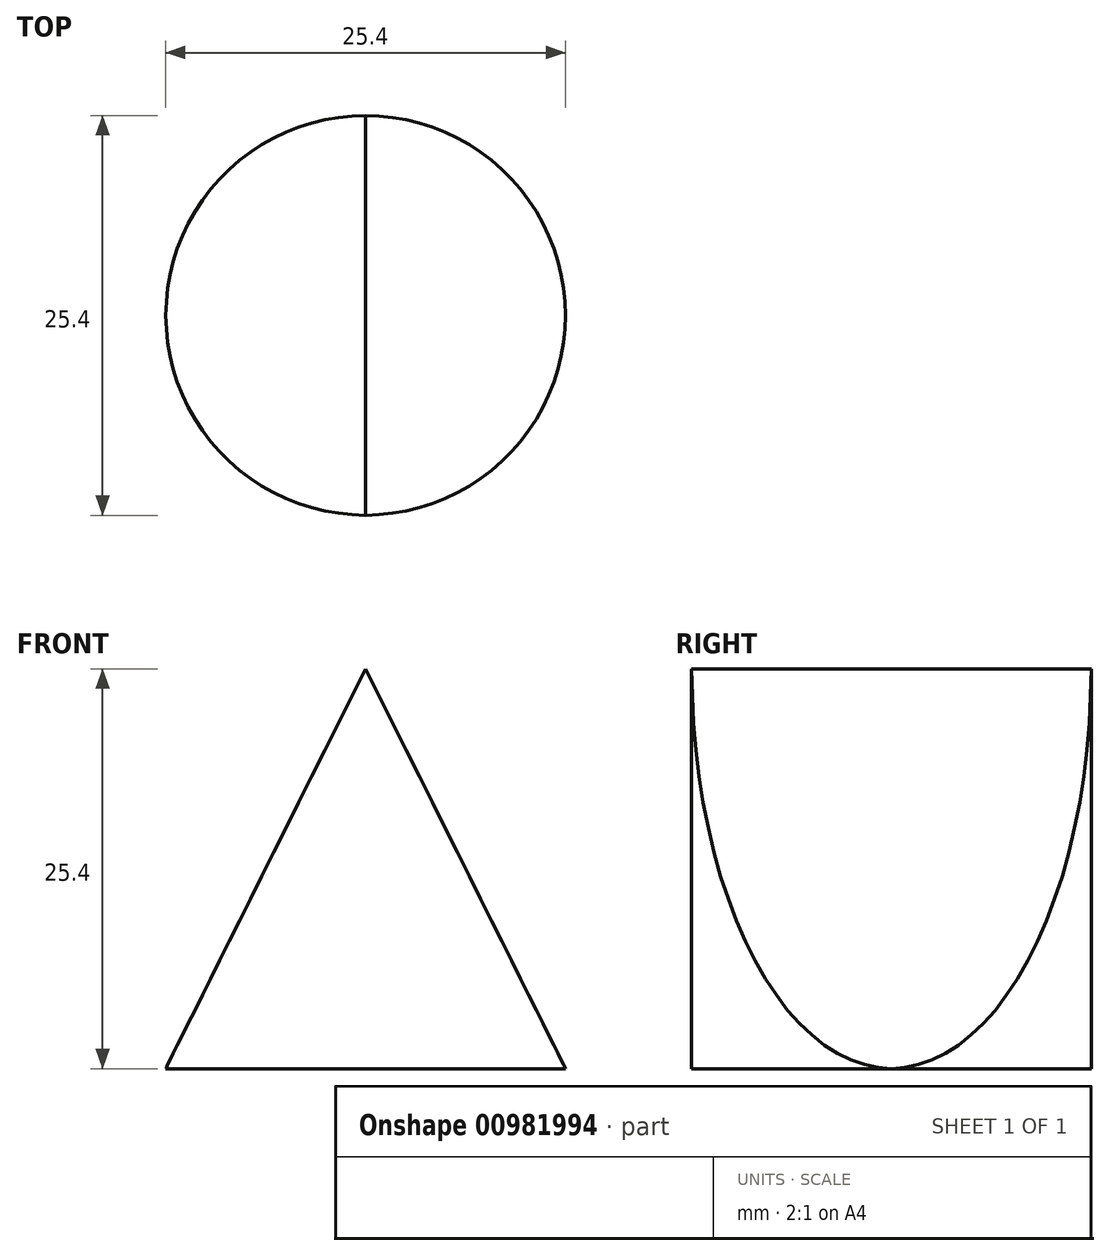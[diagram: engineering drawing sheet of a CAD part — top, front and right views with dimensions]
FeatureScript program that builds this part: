
annotation { "Feature Type Name" : "Feature", "Feature Type Description" : "" }
export const myFeature = defineFeature(function(context is Context, id is Id, definition is map)
    precondition{}
    {
        {
            var Q0;
            Q0=qCreatedBy(makeId("Top.planeOp"),FACE);
            var sketch = newSketch(context, id + "F0", { "sketchPlane" : qUnion([Q0])});
            skLineSegment(sketch, "E0.bottom", {"start": v(12.7, 12.7) * mm, "end": v(-12.7, 12.7) * mm});
            skLineSegment(sketch, "E0.top", {"start": v(12.7, -12.7) * mm, "end": v(-12.7, -12.7) * mm});
            skLineSegment(sketch, "E0.left", {"start": v(12.7, 12.7) * mm, "end": v(12.7, -12.7) * mm});
            skLineSegment(sketch, "E0.right", {"start": v(-12.7, 12.7) * mm, "end": v(-12.7, -12.7) * mm});
            skPoint(sketch, "E0.middle", {"position": v(0, 0) * mm});
            skSolve(sketch);
        }
        {
            var Q0;
            Q0 = qSketchRegion(id + "F0", true);
            extrude(context, id + "F1", {"entities" : qUnion([Q0]), "endBound" : BoundingType.SYMMETRIC, "depth" : 25.4 * mm, "offsetDistance" : 25.4 * mm});
        }
        {
            var Q0;
            Q0=qCreatedBy(makeId("Front.planeOp"),FACE);
            var sketch = newSketch(context, id + "F2", { "sketchPlane" : qUnion([Q0])});
            skLineSegment(sketch, "E1", {"start": v(0, 12.7) * mm, "end": v(-12.7, -12.7) * mm});
            skLineSegment(sketch, "E2", {"start": v(-32.9, -12.7) * mm, "end": v(-32.9, 23.98) * mm});
            skLineSegment(sketch, "E3", {"start": v(-32.9, 23.98) * mm, "end": v(-32.9, -12.7) * mm});
            skLineSegment(sketch, "E4", {"start": v(-12.7, -12.7) * mm, "end": v(-32.9, -12.7) * mm});
            skLineSegment(sketch, "E5", {"start": v(12.7, -12.7) * mm, "end": v(26.63, -12.7) * mm});
            skLineSegment(sketch, "E6", {"start": v(26.63, -12.7) * mm, "end": v(26.63, 23.98) * mm});
            skLineSegment(sketch, "E7", {"start": v(26.63, 23.98) * mm, "end": v(-32.9, 23.98) * mm});
            skLineSegment(sketch, "E8", {"start": v(0, 12.7) * mm, "end": v(12.7, -12.7) * mm});
            skSolve(sketch);
        }
        {
            var Q0;
            Q0 = qSketchRegion(id + "F2", true);
            extrude(context, id + "F3", {"entities" : qUnion([Q0]), "operationType" : NewBodyOperationType.REMOVE, "endBound" : BoundingType.SYMMETRIC, "oppositeDirection" : true, "depth" : 25.4 * mm, "offsetDistance" : 25.4 * mm});
        }
        {
            var Q0;
            Q0=qCreatedBy(makeId("Top.planeOp"),FACE);
            var sketch = newSketch(context, id + "F4", { "sketchPlane" : qUnion([Q0])});
            skCircle(sketch, "E9", {"center": v(0, 0) * mm, "radius": 26.7 * mm});
            skCircle(sketch, "E10", {"center": v(0, 0) * mm, "radius": 12.7 * mm});
            skSolve(sketch);
        }
        {
            var Q0;
            Q0 = qSketchRegion(id + "F4", true);
            extrude(context, id + "F5", {"entities" : qUnion([Q0]), "operationType" : NewBodyOperationType.REMOVE, "endBound" : BoundingType.SYMMETRIC, "oppositeDirection" : true, "depth" : 25.4 * mm, "offsetDistance" : 25.4 * mm});
        }
    });
